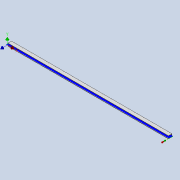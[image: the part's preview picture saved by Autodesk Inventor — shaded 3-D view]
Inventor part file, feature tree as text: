
AUTODESK INVENTOR PART (.ipt)
format: ipt  version: 2020 (Build 240168000, 168)  size: 111,104 bytes
history: native  units: mm
features: extrude x2, sketch x2
ambient origin geometry x8: Origin, YZ Plane, XZ Plane, XY Plane, X Axis, Y Axis, Z Axis, Center Point
bodies: Solid1 (feature_tree)
feature tree (4):
  extrude  "Extrusion1"  Depth=4.0mm
  extrude  "Extrusion2"  Depth=3.2mm
  sketch  "Sketch1"  dims[d0=230.0mm d1=4.0mm]
  sketch  "Sketch2"  dims[d2=5.0mm d3=0.0mm d4=3.2mm d5=4.5mm d6=0.0mm]
